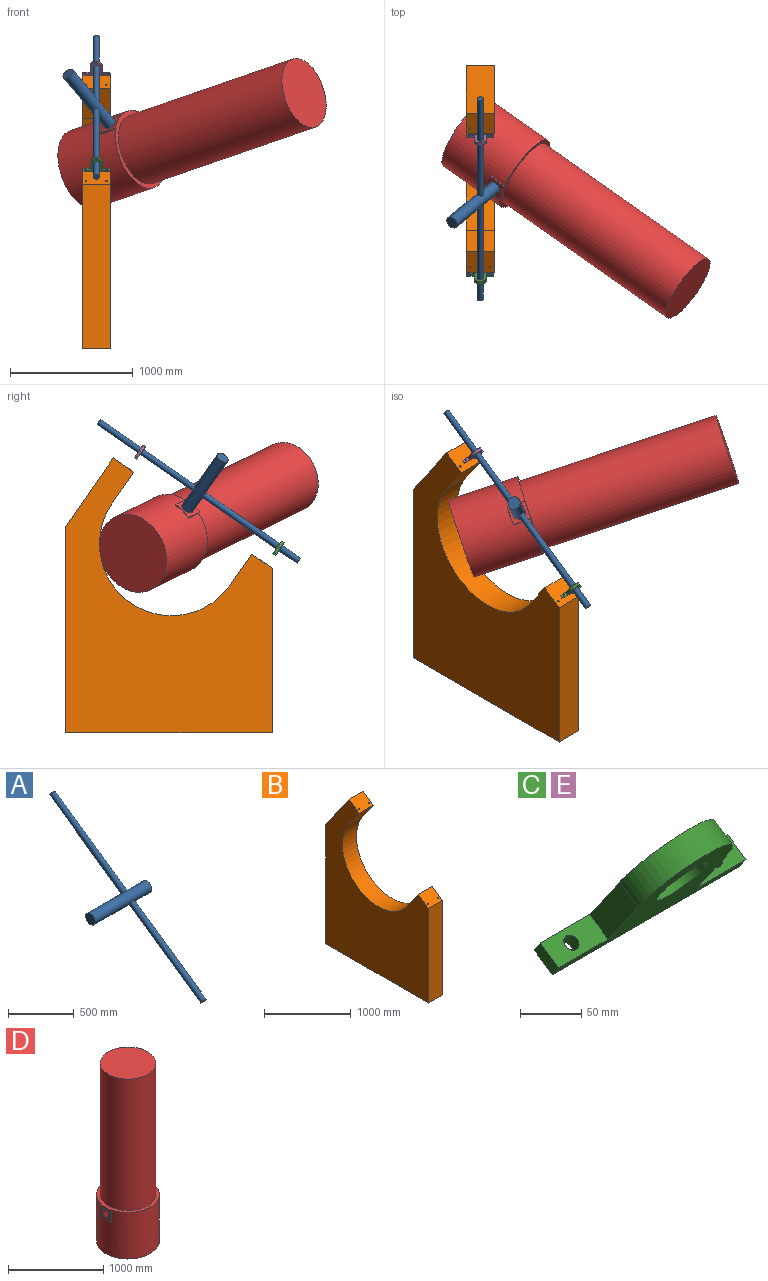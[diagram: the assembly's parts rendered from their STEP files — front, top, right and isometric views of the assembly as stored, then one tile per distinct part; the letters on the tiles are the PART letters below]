
ASSEMBLY  parts=5 mates=4
PART A: 7 faces, bbox 609.6x1656.8x1171 mm
  f0: cylinder r=25.4mm len=808.94mm, axis (0,-0.82,-0.57), area 150946.4mm2, adj f2,f4
  f1: cylinder r=25.4mm len=804.53mm, axis (0,-0.82,-0.57), area 150091.7mm2, adj f3,f4
  f2: plane 50.8x41.74mm, normal (0,0.82,0.57), area 2026.8mm2, adj f0
  f3: plane 50.8x41.74mm, normal (0,-0.82,-0.57), area 2026.8mm2, adj f1
  f4: cylinder r=50.8mm len=609.6mm, axis (-1,0,0), area 190380.1mm2, adj f0,f1,f5,f6
  f5: plane 101.6x101.6mm, normal (1,0,0), area 8107.3mm2, adj f4
  f6: plane 101.6x101.6mm, normal (-1,0,0), area 8107.3mm2, adj f4
PART B: 19 faces, bbox 228.6x1679.5x2235.2 mm
  f0: plane 1337.57x228.6mm, normal (0,-1,0), area 305768.3mm2, adj f1,f8,f9,f10
  f1: plane 1679.54x228.6mm, normal (0,0,-1), area 383943.2mm2, adj f0,f2,f9,f10
  f2: plane 1679.34x228.6mm, normal (0,1,0), area 383897.7mm2, adj f1,f3,f9,f10
  f3: plane 555.86x385.61mm, normal (0,0.82,0.57), area 154651.6mm2, adj f2,f4,f9,f10
  f4: plane 228.6x166.96mm, normal (0,-0.57,0.82), area 46165.6mm2, adj f3,f5,f9,f10,f16,f18
  f5: plane 250.44x228.6mm, normal (0,-0.82,-0.57), area 69677.3mm2, adj f4,f6,f9,f10
  f6: cylinder r=584.2mm len=1064.21mm, axis (-1,0,0), area 419553.8mm2, adj f5,f7,f9,f10
  f7: plane 250.44x228.6mm, normal (0,0.82,0.57), area 69677.3mm2, adj f6,f8,f9,f10
  f8: plane 228.6x166.96mm, normal (0,-0.57,0.82), area 46165.6mm2, adj f0,f7,f9,f10,f12,f14
  f9: plane 2235.2x1679.54mm, normal (1,0,0), area 2173978.2mm2, adj f0,f1,f2,f3,f4,f5,f6,f7
  f10: plane 2235.2x1679.54mm, normal (-1,0,0), area 2173978.2mm2, adj f0,f1,f2,f3,f4,f5,f6,f7
  f11: cone r=0mm half-angle=59deg, axis (0,-0.57,0.82), area 166.8mm2, adj f12
  f12: cylinder r=6.75mm len=16.31mm, axis (0,-0.57,0.82), area 388.7mm2, adj f8,f11
  f13: cone r=0mm half-angle=59deg, axis (0,-0.57,0.82), area 166.8mm2, adj f14
  f14: cylinder r=6.75mm len=16.31mm, axis (0,-0.57,0.82), area 388.7mm2, adj f8,f13
  f15: cone r=0mm half-angle=59deg, axis (0,-0.57,0.82), area 166.8mm2, adj f16
  f16: cylinder r=6.75mm len=28.56mm, axis (0,-0.57,0.82), area 1076.7mm2, adj f4,f15
  f17: cone r=0mm half-angle=59deg, axis (0,-0.57,0.82), area 166.8mm2, adj f18
  f18: cylinder r=6.75mm len=28.56mm, axis (0,-0.57,0.82), area 1076.7mm2, adj f4,f17
PART C: 13 faces, bbox 215.9x91.2x115.9 mm
  f0: plane 28.11x24.91mm, normal (1,0,0), area 322.6mm2, adj f1,f7,f9,f10
  f1: plane 215.9x20.87mm, normal (0,0.57,-0.82), area 5197.9mm2, adj f0,f2,f9,f10,f11,f12
  f2: plane 28.11x24.91mm, normal (-1,0,0), area 322.6mm2, adj f1,f3,f9,f10
  f3: plane 57.15x20.87mm, normal (0,-0.57,0.82), area 1308.6mm2, adj f2,f4,f9,f10,f12
  f4: plane 63.75x55.05mm, normal (-1,0,0), area 1523.2mm2, adj f3,f5,f9,f10
  f5: cylinder r=50.8mm len=101.6mm, axis (0,-0.82,-0.57), area 4053.7mm2, adj f4,f6,f9,f10
  f6: plane 63.75x55.05mm, normal (1,0,0), area 1523.2mm2, adj f5,f7,f9,f10
  f7: plane 57.15x20.87mm, normal (0,-0.57,0.82), area 1308.6mm2, adj f0,f6,f9,f10,f11
  f8: cylinder r=25.4mm len=56.22mm, axis (0,-0.82,-0.57), area 4053.7mm2, adj f9,f10
  f9: plane 215.9x101.45mm, normal (0,0.82,0.57), area 10861.7mm2, adj f0,f1,f2,f3,f4,f5,f6,f7
  f10: plane 215.9x101.45mm, normal (0,-0.82,-0.57), area 10861.7mm2, adj f0,f1,f2,f3,f4,f5,f6,f7
  f11: cylinder r=6.75mm len=18.33mm, axis (0,-0.57,0.82), area 538.3mm2, adj f1,f7
  f12: cylinder r=6.75mm len=18.33mm, axis (0,-0.57,0.82), area 538.3mm2, adj f1,f3
PART D: 11 faces, bbox 664.2x660.4x2286 mm
  f0: cylinder r=330.2mm len=660.4mm, axis (0,0,-1), area 1214956.1mm2, adj f1,f2,f3,f5,f6
  f1: plane 664.19x660.4mm, normal (0,0,1), area 75513.5mm2, adj f0,f3,f4,f5,f7
  f2: plane 660.4x660.4mm, normal (0,0,-1), area 342534.3mm2, adj f0
  f3: plane 152.4x12.7mm, normal (0,1,0), area 1935.5mm2, adj f0,f1,f4,f6
  f4: plane 152.4x152.4mm, normal (-1,0,0), area 15118.4mm2, adj f1,f3,f5,f6,f10
  f5: plane 152.4x12.7mm, normal (0,-1,0), area 1935.5mm2, adj f0,f1,f4,f6
  f6: plane 152.4x12.7mm, normal (0,0,-1), area 1027.5mm2, adj f0,f3,f4,f5
  f7: cylinder r=292.1mm len=1689.1mm, axis (0,0,-1), area 3100036.4mm2, adj f1,f8
  f8: plane 584.2x584.2mm, normal (0,0,1), area 268048.3mm2, adj f7
  f9: cone r=0mm half-angle=59deg, axis (-1,0,0), area 9458.3mm2, adj f10
  f10: cylinder r=50.8mm len=101.6mm, axis (-1,0,0), area 1216.1mm2, adj f4,f9
PART E: same geometry as C
PLACE A rot(axis=(0,0.82,0.57),55.6deg) t=(-920.12,-401.23,578.4)mm
PLACE B at identity fixed
PLACE C t=(0,-55.9,80.58)mm
PLACE D rot(axis=(0.64,0.76,0.12),74.8deg) t=(-592.85,539.15,1981.76)mm
PLACE E t=(0,1071.07,862.39)mm
MATE revolute D.f9 <-> A.f4  axis (-0.56,-0.47,0.68) through (229.05,690.18,1824.37)mm
MATE fastened E.f12 <-> B.f17  axis (0,0.57,-0.82) through (31.75,1110.8,2231.81)mm
MATE revolute A.f0 <-> C.f5  axis (0,-0.82,-0.57) through (114.3,-217.12,1399.04)mm
MATE fastened C.f11 <-> B.f12  axis (0,0.57,-0.82) through (196.85,-16.17,1450)mm
